FCSTD DOCUMENT  (FreeCAD 1.0R39319 (Git))
Label: Week1Assignment1
License: All rights reserved
LicenseURL: https://en.wikipedia.org/wiki/All_rights_reserved
objects: Sketcher::SketchObject×1
note: 2 computed .brp shape members not serialized (recipe doc carries the construction recipe); baked Part::Feature solids carry a one-line shape summary decoded from their .brp

FEATURE [Sketcher::SketchObject] Sketch
  ArcFitTolerance = 1e-06
  FullyConstrained = true
  MakeInternals = false
  sketch-geometry (14):
    g0: Circle CenterX=0 CenterY=0 CenterZ=0 NormalX=0 NormalY=0 NormalZ=1 AngleXU=0 Radius=30
    g1: Circle CenterX=0 CenterY=0 CenterZ=0 NormalX=0 NormalY=0 NormalZ=1 AngleXU=0 Radius=8
    g2: Circle [constr] CenterX=0 CenterY=0 CenterZ=0 NormalX=0 NormalY=0 NormalZ=1 AngleXU=0 Radius=20
    g3: Circle CenterX=0 CenterY=20 CenterZ=0 NormalX=0 NormalY=0 NormalZ=1 AngleXU=0 Radius=5
    g4: Circle CenterX=0 CenterY=-20 CenterZ=0 NormalX=0 NormalY=0 NormalZ=1 AngleXU=0 Radius=5
    g5: Circle CenterX=-20 CenterY=0 CenterZ=0 NormalX=0 NormalY=0 NormalZ=1 AngleXU=0 Radius=5
    g6: Circle CenterX=20 CenterY=0 CenterZ=0 NormalX=0 NormalY=0 NormalZ=1 AngleXU=0 Radius=5
    g7: Circle CenterX=-55.9274 CenterY=-70 CenterZ=0 NormalX=0 NormalY=0 NormalZ=1 AngleXU=0 Radius=15
    g8: Circle CenterX=-55.9274 CenterY=-70 CenterZ=0 NormalX=0 NormalY=0 NormalZ=1 AngleXU=0 Radius=10
    g9: Circle CenterX=55.9274 CenterY=-70 CenterZ=0 NormalX=0 NormalY=0 NormalZ=1 AngleXU=0 Radius=15
    g10: Circle CenterX=55.9274 CenterY=-70 CenterZ=0 NormalX=0 NormalY=0 NormalZ=1 AngleXU=0 Radius=10
    g11: ArcOfCircle CenterX=0 CenterY=-119.971 CenterZ=0 NormalX=0 NormalY=0 NormalZ=1 AngleXU=0 Radius=60 StartAngle=0.729214 EndAngle=2.41238
    g12: LineSegment StartX=-69.0485 StartY=-62.731 StartZ=0 EndX=-26.2421 EndY=14.5379 EndZ=0
    g13: LineSegment StartX=69.0485 StartY=-62.731 StartZ=0 EndX=26.2421 EndY=14.5379 EndZ=0
  constraints (32):
    c: Diameter(g0) = 60
    c: Coincident(g0,g-1)
    c: Coincident(g1,g0)
    c: Diameter(g1) = 16
    c: Diameter(g2) = 40
    c: Coincident(g2,g0)
    c: Diameter(g3) = 10
    c: PointOnObject(g3,g-2)
    c: PointOnObject(g3,g2)
    c: Diameter(g4) = 10
    c: Block(g4)
    c: Diameter(g5) = 10
    c: PointOnObject(g5,g-1)
    c: PointOnObject(g5,g2)
    c: Diameter(g6) = 10
    c: Block(g6)
    c: Diameter(g7) = 30
    c: Diameter(g8) = 20
    c: Coincident(g8,g7)
    c: Diameter(g9) = 30
    c: Diameter(g10) = 20
    c: Coincident(g10,g9)
    c: Block(g7)
    c: Block(g8)
    c: Block(g9)
    c: Diameter(g11) = 120
    c: PointOnObject(g11,g-2)
    c: Tangent(g11,g7) = 1.5708
    c: Tangent(g11,g9) = 1.5708
    c: Tangent(g12,g7) = 1.5708
    c: Tangent(g12,g0) = 1.5708
    c: Block(g13)
